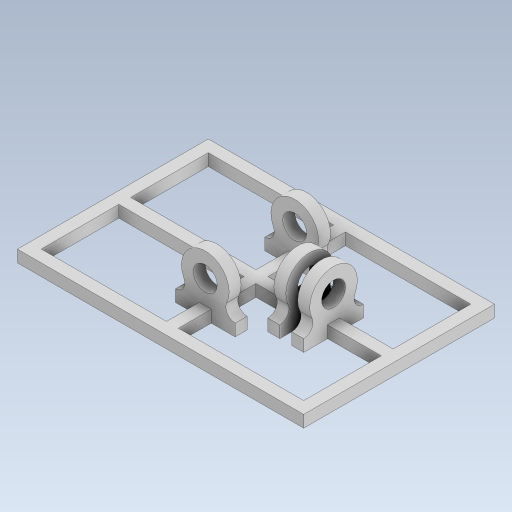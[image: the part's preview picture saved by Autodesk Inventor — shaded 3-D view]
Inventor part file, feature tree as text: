
AUTODESK INVENTOR PART (.ipt)
format: ipt  version: 2023 (Build 270158000, 158)  size: 243,200 bytes
history: native  units: in
note: dims shown in document units (in); Inventor stores cm internally (conversion verified against a paired STEP export)
features: extrude x3, sketch x3, mirror x1, pattern_linear x1
ambient origin geometry x8: Origin, YZ Plane, XZ Plane, XY Plane, X Axis, Y Axis, Z Axis, Center Point
bodies: Solid1 (feature_tree)
feature tree (8):
  extrude  "Extrusion1"  Depth=0.25in
  extrude  "Extrusion2"  Depth=0.25in
  mirror  "Mirror1"
  extrude  "Extrusion3"  Depth=4.0in
  pattern_linear  "Rectangular Pattern1"  Spacing1=6.0in  [1 undecoded]
  sketch  "Sketch1"  dims[d0=0.25in d1=0.25in]
  sketch  "Sketch2"  dims[d2=0.25in d3=0.25in]
  sketch  "Sketch3"  dims[d4=0.25in d5=4.0in d6=6.0in d7=0.25in d8=1.25in d9=0.25in d10=0.25in d11=0.0in d12=1.0in d13=0.5in d14=0.5in d15=1.0in d16=1.25in d17=0.25in d18=0.0in d20=0.5in d22=1.25in d23=1.0in d24=0.0in d25=0.0in d26=0.7874in d28=0.5in d27=0.0344in]
note: 1 required parameter value undecoded (feature->parameter linkage not recoverable at this tier; creation-order binding heuristic only, values carry confidence <= 0.55)
